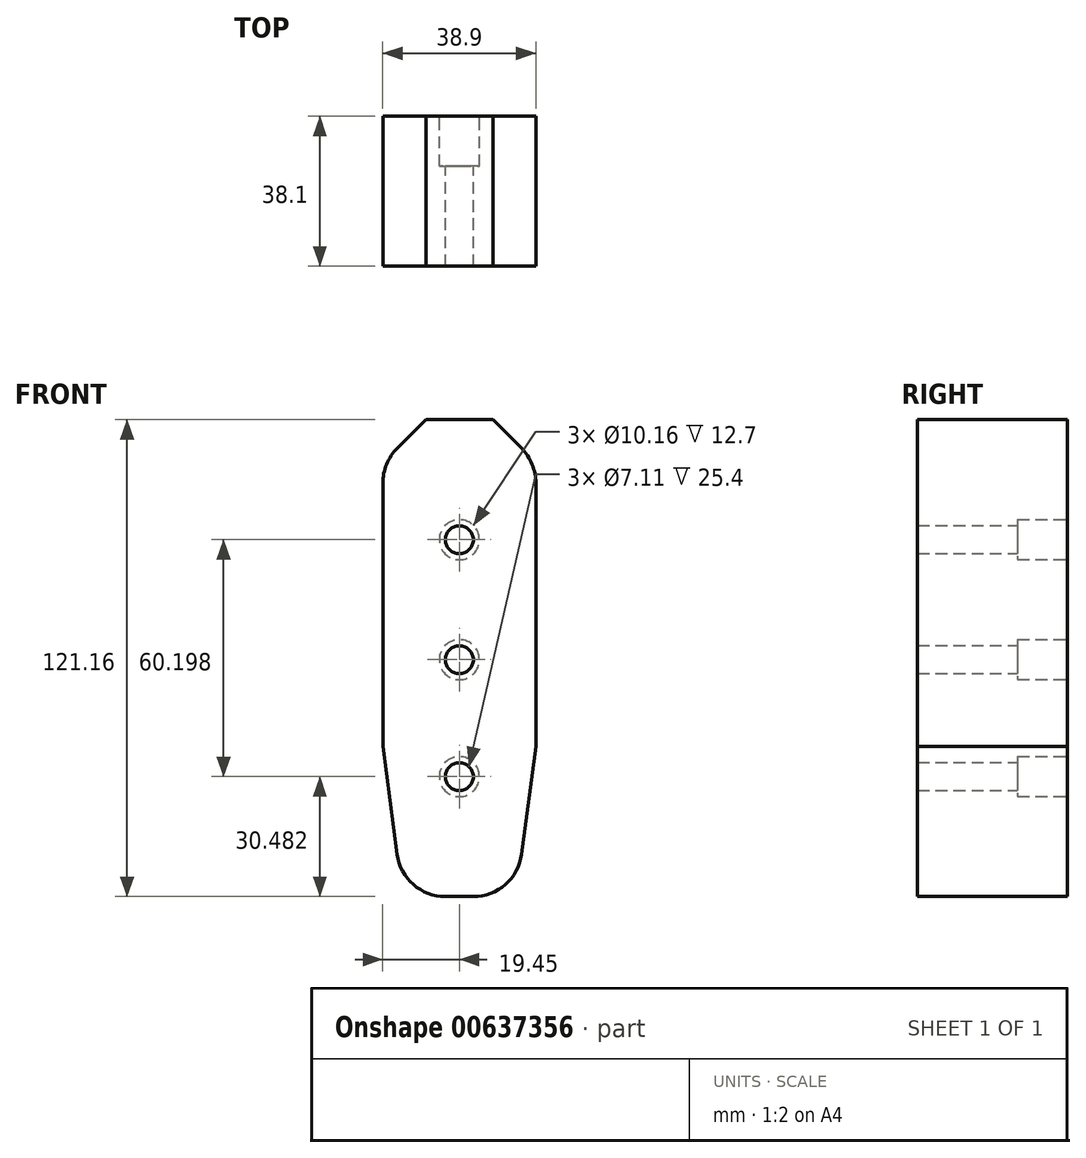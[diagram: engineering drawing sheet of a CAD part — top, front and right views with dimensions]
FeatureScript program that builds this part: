
annotation { "Feature Type Name" : "Feature", "Feature Type Description" : "" }
export const myFeature = defineFeature(function(context is Context, id is Id, definition is map)
    precondition{}
    {
        {
            var Q0;
            Q0=qCreatedBy(makeId("Front.planeOp"),FACE);
            var sketch = newSketch(context, id + "F0", { "sketchPlane" : qUnion([Q0])});
            skLineSegment(sketch, "E0", {"start": v(19.45, 50.8) * mm, "end": v(-19.45, 50.8) * mm});
            skLineSegment(sketch, "E1", {"start": v(19.45, 50.8) * mm, "end": v(19.45, -70.36) * mm});
            skLineSegment(sketch, "E2", {"start": v(-19.45, 50.8) * mm, "end": v(-19.45, -70.36) * mm});
            skLineSegment(sketch, "E3", {"start": v(19.45, -70.36) * mm, "end": v(-19.45, -70.36) * mm});
            skSolve(sketch);
        }
        {
            var Q0;
            Q0=qSketchRegion(id+"F0",true);
            extrude(context, id + "F1", {"entities" : qUnion([Q0]), "oppositeDirection" : true, "depth" : 38.1 * mm, "offsetDistance" : 25.4 * mm});
        }
        {
            var Q0;
            Q0=makeQuery(id+"F1.opExtrude","SWEPT_EDGE",EDGE,{"disambiguationData":[OSD([sQuery(id+"F0.wireOp",EDGE,"5a9edbc7-dbc8-452a-a94e-e9a3c7398107"),sQuery(id+"F0.wireOp",EDGE,"E0")])]});
            var Q1;
            Q1=makeQuery(id+"F1.opExtrude","SWEPT_EDGE",EDGE,{"disambiguationData":[OSD([sQuery(id+"F0.wireOp",EDGE,"E0"),sQuery(id+"F0.wireOp",EDGE,"e4f6d671-606f-493e-a44e-61b159010204")])]});
            chamfer(context, id + "F2", {"entities" : qUnion([Q0, Q1]), "width" : 10.92 * mm, "tangentPropagation" : true});
        }
        {
            var Q0;
            {var subQ0=sQuery(id+"F0.wireOp",EDGE,"E1");Q0=makeQuery(id+"F2.opChamfer","BLEND_EDGE",EDGE,{"blendedFrom":[makeQuery(id+"F1.opExtrude","SWEPT_EDGE",EDGE,{"disambiguationData":[OSD([sQuery(id+"F0.wireOp",EDGE,"E0"),subQ0])]}),makeQuery(id+"F1.opExtrude","SWEPT_FACE",FACE,{"disambiguationData":[OSD([subQ0])]})],"blendedInto":[makeQuery(id+"F1.opExtrude","SWEPT_FACE",FACE,{"disambiguationData":[OSD([subQ0])]})]});}
            var Q1;
            {var subQ0=sQuery(id+"F0.wireOp",EDGE,"E2");Q1=makeQuery(id+"F2.opChamfer","BLEND_EDGE",EDGE,{"blendedFrom":[makeQuery(id+"F1.opExtrude","SWEPT_EDGE",EDGE,{"disambiguationData":[OSD([sQuery(id+"F0.wireOp",EDGE,"E0"),subQ0])]}),makeQuery(id+"F1.opExtrude","SWEPT_FACE",FACE,{"disambiguationData":[OSD([subQ0])]})],"blendedInto":[makeQuery(id+"F1.opExtrude","SWEPT_FACE",FACE,{"disambiguationData":[OSD([subQ0])]})]});}
            fillet(context, id + "F3", {"entities" : qUnion([Q0, Q1]), "radius" : 12.7 * mm, "tangentPropagation" : true, "allowEdgeOverflow" : false});
        }
        {
            var Q0;
            Q0=makeQuery(id+"F1.opExtrude","SWEPT_EDGE",EDGE,{"disambiguationData":[OSD([sQuery(id+"F0.wireOp",EDGE,"E2"),sQuery(id+"F0.wireOp",EDGE,"E3")])]});
            var Q1;
            Q1=makeQuery(id+"F1.opExtrude","SWEPT_EDGE",EDGE,{"disambiguationData":[OSD([sQuery(id+"F0.wireOp",EDGE,"E1"),sQuery(id+"F0.wireOp",EDGE,"E3")])]});
            chamfer(context, id + "F4", {"entities" : qUnion([Q0, Q1]), "chamferType" : ChamferType.TWO_OFFSETS, "width1" : 38.1 * mm, "oppositeDirection" : false, "width2" : 5.08 * mm, "tangentPropagation" : true});
        }
        {
            var Q0;
            {var subQ0=sQuery(id+"F0.wireOp",EDGE,"E3");Q0=makeQuery(id+"F4.opChamfer","BLEND_EDGE",EDGE,{"blendedFrom":[makeQuery(id+"F1.opExtrude","SWEPT_EDGE",EDGE,{"disambiguationData":[OSD([sQuery(id+"F0.wireOp",EDGE,"E1"),subQ0])]}),makeQuery(id+"F1.opExtrude","SWEPT_FACE",FACE,{"disambiguationData":[OSD([subQ0])]})],"blendedInto":[makeQuery(id+"F1.opExtrude","SWEPT_FACE",FACE,{"disambiguationData":[OSD([subQ0])]})]});}
            var Q1;
            {var subQ0=sQuery(id+"F0.wireOp",EDGE,"E3");Q1=makeQuery(id+"F4.opChamfer","BLEND_EDGE",EDGE,{"blendedFrom":[makeQuery(id+"F1.opExtrude","SWEPT_EDGE",EDGE,{"disambiguationData":[OSD([sQuery(id+"F0.wireOp",EDGE,"E2"),subQ0])]}),makeQuery(id+"F1.opExtrude","SWEPT_FACE",FACE,{"disambiguationData":[OSD([subQ0])]})],"blendedInto":[makeQuery(id+"F1.opExtrude","SWEPT_FACE",FACE,{"disambiguationData":[OSD([subQ0])]})]});}
            fillet(context, id + "F5", {"entities" : qUnion([Q0, Q1]), "radius" : 12.38 * mm, "tangentPropagation" : true, "allowEdgeOverflow" : false});
        }
        {
            var Q0;
            Q0=makeQuery(id+"F1.opExtrude","CAP_FACE",FACE,{"disambiguationData":[OSD([sQuery(id+"F0.wireOp",EDGE,"E0"),sQuery(id+"F0.wireOp",EDGE,"E1"),sQuery(id+"F0.wireOp",EDGE,"E2"),sQuery(id+"F0.wireOp",EDGE,"E3")])],"isStart":false});
            var sketch = newSketch(context, id + "F6", { "sketchPlane" : qUnion([Q0])});
            skCircle(sketch, "E4", {"center": v(0, -39.88) * mm, "radius": 5.08 * mm});
            skCircle(sketch, "E5", {"center": v(0, -10.16) * mm, "radius": 5.08 * mm});
            skCircle(sketch, "E6", {"center": v(0, 20.32) * mm, "radius": 5.08 * mm});
            skCircle(sketch, "E7", {"center": v(0, -10.16) * mm, "radius": 3.56 * mm});
            skCircle(sketch, "E8", {"center": v(0, 20.32) * mm, "radius": 3.56 * mm});
            skCircle(sketch, "E9", {"center": v(0, -39.88) * mm, "radius": 3.56 * mm});
            skSolve(sketch);
        }
        {
            var Q0;
            Q0=qSketchRegion(id+"F6",true);
            extrude(context, id + "F7", {"entities" : qUnion([Q0]), "operationType" : NewBodyOperationType.REMOVE, "oppositeDirection" : true, "depth" : 12.7 * mm, "offsetDistance" : 25.4 * mm});
        }
        {
            var Q0;
            Q0=makeQuery(id+"F6.imprint","IMPRINT",FACE,{"disambiguationData":[TD([[makeQuery(id+"F6.imprint","IMPRINT",EDGE,{"derivedFrom":sQuery(id+"F6.wireOp",EDGE,"E8")}),1.0]])]});
            var Q1;
            Q1=makeQuery(id+"F6.imprint","IMPRINT",FACE,{"disambiguationData":[TD([[makeQuery(id+"F6.imprint","IMPRINT",EDGE,{"derivedFrom":sQuery(id+"F6.wireOp",EDGE,"E7")}),1.0]])]});
            var Q2;
            Q2=makeQuery(id+"F6.imprint","IMPRINT",FACE,{"disambiguationData":[TD([[makeQuery(id+"F6.imprint","IMPRINT",EDGE,{"derivedFrom":sQuery(id+"F6.wireOp",EDGE,"E9")}),1.0]])]});
            extrude(context, id + "F8", {"entities" : qUnion([Q0, Q1, Q2]), "operationType" : NewBodyOperationType.REMOVE, "endBound" : BoundingType.THROUGH_ALL, "oppositeDirection" : true, "depth" : 25.4 * mm, "offsetDistance" : 25.4 * mm});
        }
    });
